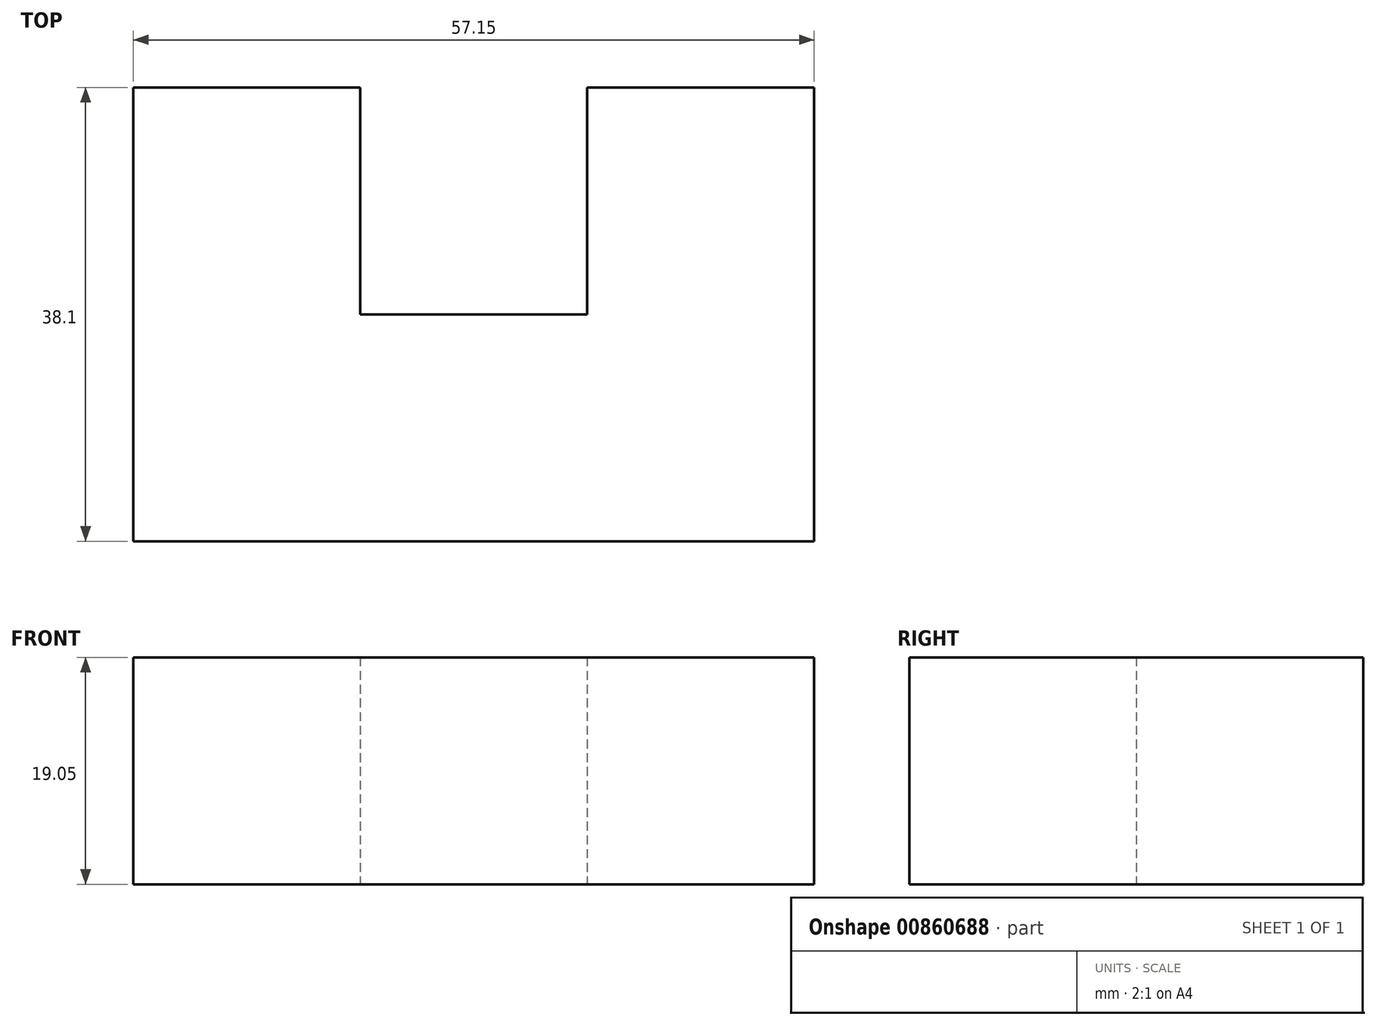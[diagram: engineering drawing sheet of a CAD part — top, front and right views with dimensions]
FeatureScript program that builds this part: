
annotation { "Feature Type Name" : "Feature", "Feature Type Description" : "" }
export const myFeature = defineFeature(function(context is Context, id is Id, definition is map)
    precondition{}
    {
        {
            var Q0;
            Q0=qCreatedBy(makeId("Top.planeOp"),FACE);
            var sketch = newSketch(context, id + "F0", { "sketchPlane" : qUnion([Q0])});
            skLineSegment(sketch, "E0", {"start": v(0, 0) * mm, "end": v(0, -38.1) * mm});
            skLineSegment(sketch, "E1", {"start": v(0, -38.1) * mm, "end": v(57.15, -38.1) * mm});
            skLineSegment(sketch, "E2", {"start": v(57.15, -38.1) * mm, "end": v(57.15, 0) * mm});
            skLineSegment(sketch, "E3", {"start": v(57.15, 0) * mm, "end": v(38.1, 0) * mm});
            skLineSegment(sketch, "E4", {"start": v(38.1, 0) * mm, "end": v(38.1, -19.05) * mm});
            skLineSegment(sketch, "E5", {"start": v(38.1, -19.05) * mm, "end": v(19.05, -19.05) * mm});
            skLineSegment(sketch, "E6", {"start": v(19.05, -19.05) * mm, "end": v(19.05, 0) * mm});
            skLineSegment(sketch, "E7", {"start": v(19.05, 0) * mm, "end": v(0, 0) * mm});
            skSolve(sketch);
        }
        {
            var Q0;
            Q0 = qSketchRegion(id + "F0", true);
            extrude(context, id + "F1", {"entities" : qUnion([Q0]), "depth" : 19.05 * mm, "offsetDistance" : 25.4 * mm});
        }
    });
